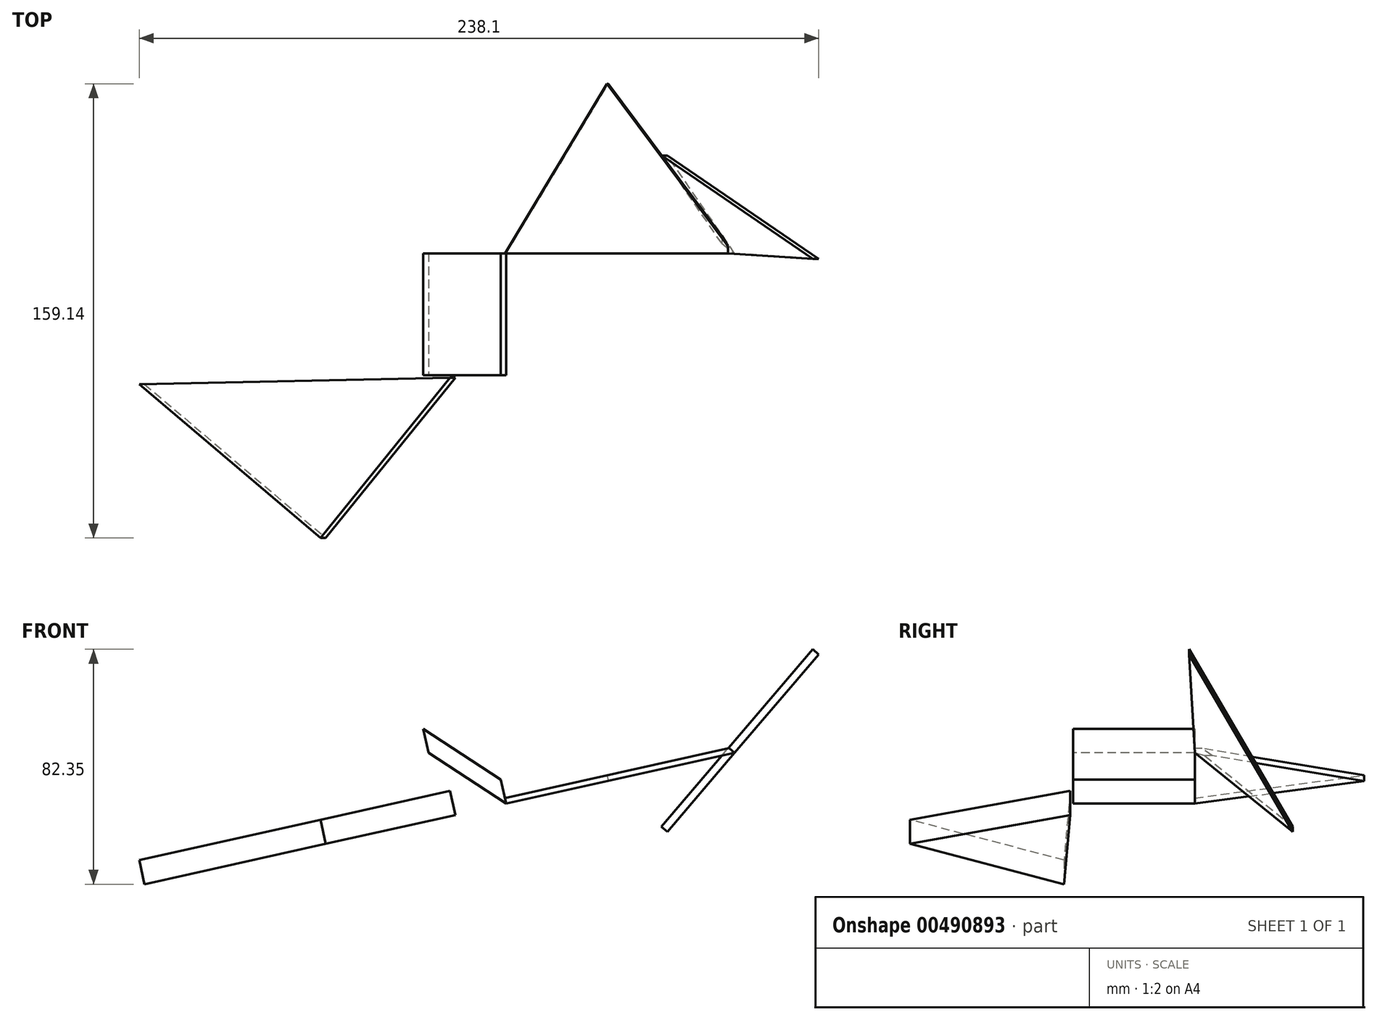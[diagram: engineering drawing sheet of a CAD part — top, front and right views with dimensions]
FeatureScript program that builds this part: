
annotation { "Feature Type Name" : "Feature", "Feature Type Description" : "" }
export const myFeature = defineFeature(function(context is Context, id is Id, definition is map)
    precondition{}
    {
        {
            var Q0;
            Q0=qCreatedBy(makeId("Front.planeOp"),FACE);
            var sketch = newSketch(context, id + "F0", { "sketchPlane" : qUnion([Q0])});
            skLineSegment(sketch, "E0", {"start": v(0, 0) * mm, "end": v(35.12, 54.7) * mm});
            skLineSegment(sketch, "E1", {"start": v(35.12, 54.7) * mm, "end": v(115.17, 71.38) * mm});
            skLineSegment(sketch, "E2", {"start": v(115.17, 71.38) * mm, "end": v(144.62, 28.91) * mm});
            skLineSegment(sketch, "E3", {"start": v(144.62, 28.91) * mm, "end": v(144.62, -21.32) * mm});
            skLineSegment(sketch, "E4", {"start": v(144.62, -21.32) * mm, "end": v(115.17, -55.82) * mm});
            skLineSegment(sketch, "E5", {"start": v(115.17, -55.82) * mm, "end": v(35.12, -73.64) * mm});
            skLineSegment(sketch, "E6", {"start": v(35.12, -73.64) * mm, "end": v(7.93, -55.82) * mm});
            skLineSegment(sketch, "E7", {"start": v(7.93, -55.82) * mm, "end": v(0, 0) * mm});
            skSolve(sketch);
        }
        {
            var Q0;
            Q0 = qSketchRegion(id + "F0", true);
            var Q1;
            Q1=sQuery(id+"F0.wireOp",EDGE,"E1");
            var Q2;
            Q2=sQuery(id+"F0.wireOp",EDGE,"E2");
            var Q3;
            Q3=sQuery(id+"F0.wireOp",EDGE,"E3");
            var Q4;
            Q4=sQuery(id+"F0.wireOp",EDGE,"E4");
            var Q5;
            Q5=sQuery(id+"F0.wireOp",EDGE,"E5");
            var Q6;
            Q6=sQuery(id+"F0.wireOp",EDGE,"E6");
            var Q7;
            Q7=sQuery(id+"F0.wireOp",EDGE,"E7");
            var Q8;
            Q8=sQuery(id+"F0.wireOp",EDGE,"E0");
            extrude(context, id + "F1", {"entities" : qUnion([Q0]), "bodyType" : ToolBodyType.SURFACE, "surfaceEntities" : qUnion([Q1, Q2, Q3, Q4, Q5, Q6, Q7, Q8]), "depth" : 42.67 * mm});
        }
        {
            var Q0;
            Q0=makeQuery(id+"F1.opExtrude","SWEPT_FACE",FACE,{"disambiguationData":[OSD([sQuery(id+"F0.wireOp",EDGE,"E5")])]});
            var sketch = newSketch(context, id + "F2", { "sketchPlane" : qUnion([Q0])});
            skLineSegment(sketch, "E8", {"start": v(-111.55, -45.83) * mm, "end": v(-46.5, -99.74) * mm});
            skLineSegment(sketch, "E9", {"start": v(-46.5, -99.74) * mm, "end": v(0, -43.64) * mm});
            skLineSegment(sketch, "E10", {"start": v(0, -43.64) * mm, "end": v(-111.55, -45.83) * mm});
            skSolve(sketch);
        }
        {
            var Q0;
            Q0=makeQuery(id+"F2.imprint","IMPRINT",FACE,{"disambiguationData":[TD([[makeQuery(id+"F2.imprint","IMPRINT",EDGE,{"derivedFrom":sQuery(id+"F2.wireOp",EDGE,"E8")}),1.0]])]});
            var Q1;
            Q1=makeQuery(id+"F1.opExtrude","SWEPT_FACE",FACE,{"disambiguationData":[OSD([sQuery(id+"F0.wireOp",EDGE,"E6")])]});
            extrude(context, id + "F3", {"entities" : qUnion([Q0, Q1]), "depth" : 8.64 * mm});
        }
        {
            var Q0;
            Q0=makeQuery(id+"F1.opExtrude","SWEPT_FACE",FACE,{"disambiguationData":[OSD([sQuery(id+"F0.wireOp",EDGE,"E5")])]});
            var sketch = newSketch(context, id + "F4", { "sketchPlane" : qUnion([Q0])});
            skLineSegment(sketch, "E11", {"start": v(18.27, 0) * mm, "end": v(54.94, 59.4) * mm});
            skLineSegment(sketch, "E12", {"start": v(54.94, 59.4) * mm, "end": v(100.29, 0) * mm});
            skLineSegment(sketch, "E13", {"start": v(-186.85, 29.97) * mm, "end": v(54.94, 59.4) * mm});
            skLineSegment(sketch, "E14", {"start": v(-461.43, 75.8) * mm, "end": v(54.94, 59.4) * mm});
            skLineSegment(sketch, "E15", {"start": v(-680.82, 120.14) * mm, "end": v(54.94, 59.4) * mm});
            skSolve(sketch);
        }
        {
            var Q0;
            Q0 = qSketchRegion(id + "F4", true);
            var Q1;
            Q1=makeQuery(id+"F4.imprint","IMPRINT",FACE,{"disambiguationData":[TD([[makeQuery(id+"F4.imprint","IMPRINT",EDGE,{"derivedFrom":sQuery(id+"F4.wireOp",EDGE,"E11")}),-1.0]])]});
            extrude(context, id + "F5", {"entities" : qUnion([Q0, Q1]), "depth" : 2.03 * mm});
        }
        {
            var Q0;
            Q0=makeQuery(id+"F1.opExtrude","SWEPT_FACE",FACE,{"disambiguationData":[OSD([sQuery(id+"F0.wireOp",EDGE,"E4")])]});
            var sketch = newSketch(context, id + "F6", { "sketchPlane" : qUnion([Q0])});
            skLineSegment(sketch, "E16", {"start": v(-34.3, -4.04) * mm, "end": v(1.98, 77.69) * mm});
            skLineSegment(sketch, "E17", {"start": v(1.98, 77.69) * mm, "end": v(0, 32.33) * mm});
            skLineSegment(sketch, "E18", {"start": v(0, 32.33) * mm, "end": v(-34.3, -4.04) * mm});
            skSolve(sketch);
        }
        {
            var Q0;
            Q0 = qSketchRegion(id + "F6", true);
            extrude(context, id + "F7", {"entities" : qUnion([Q0]), "operationType" : NewBodyOperationType.ADD, "depth" : 2.8 * mm});
        }
    });
